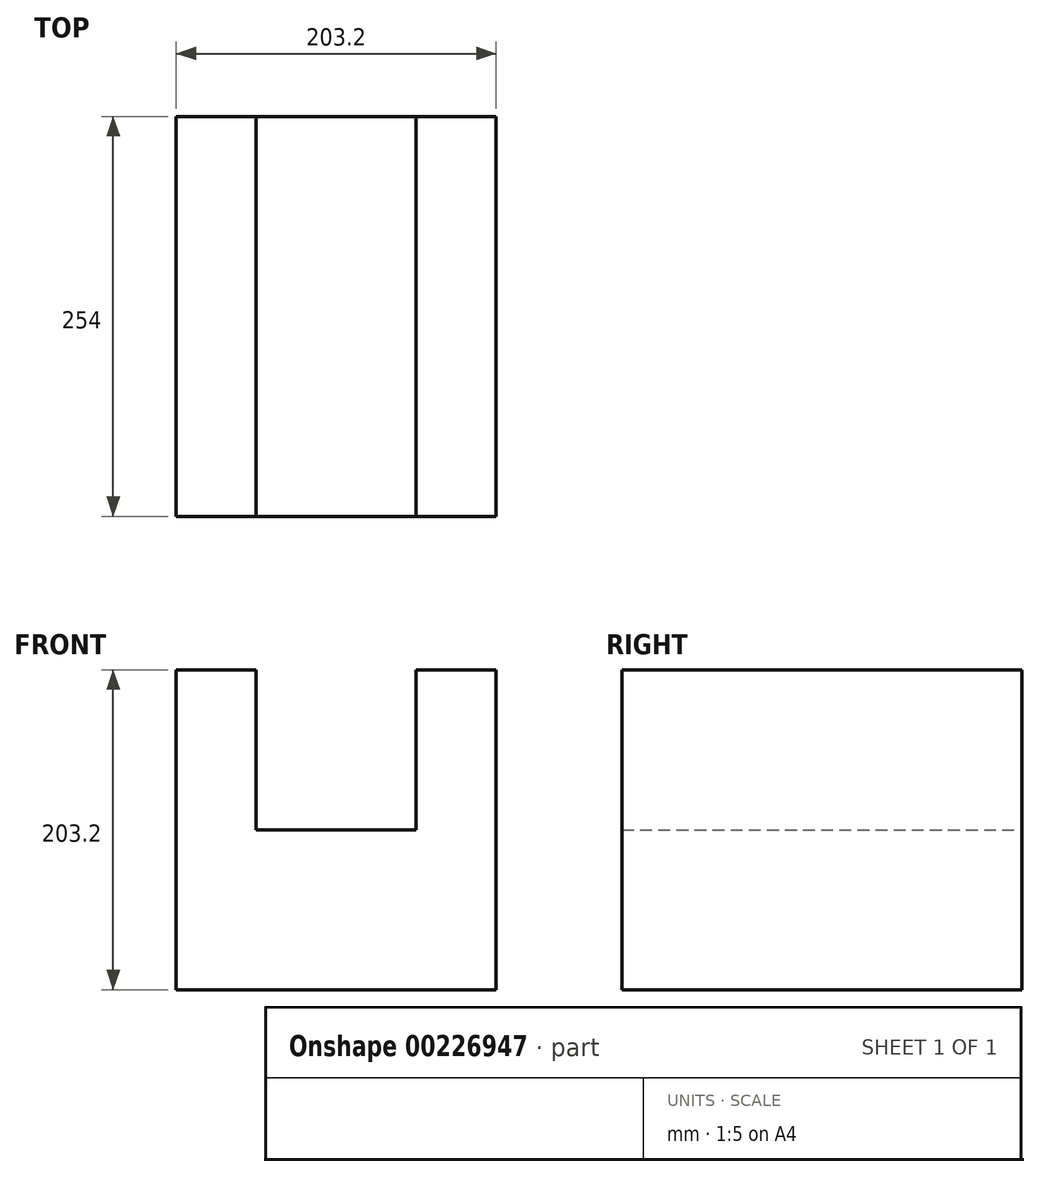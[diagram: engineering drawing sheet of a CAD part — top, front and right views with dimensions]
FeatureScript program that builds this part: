
annotation { "Feature Type Name" : "Feature", "Feature Type Description" : "" }
export const myFeature = defineFeature(function(context is Context, id is Id, definition is map)
    precondition{}
    {
        {
            var Q0;
            Q0=qCreatedBy(makeId("Front.planeOp"),FACE);
            var sketch = newSketch(context, id + "F0", { "sketchPlane" : qUnion([Q0])});
            skLineSegment(sketch, "E0", {"start": v(106.3, 82.24) * mm, "end": v(106.3, -120.96) * mm});
            skLineSegment(sketch, "E1", {"start": v(106.3, 82.24) * mm, "end": v(55.5, 82.24) * mm});
            skLineSegment(sketch, "E2", {"start": v(-96.9, 82.24) * mm, "end": v(-96.9, -120.96) * mm});
            skLineSegment(sketch, "E3", {"start": v(-96.9, -120.96) * mm, "end": v(106.3, -120.96) * mm});
            skLineSegment(sketch, "E4", {"start": v(-46.1, 82.24) * mm, "end": v(-46.1, -19.36) * mm});
            skLineSegment(sketch, "E5", {"start": v(55.5, 82.24) * mm, "end": v(55.5, -19.36) * mm});
            skLineSegment(sketch, "E6", {"start": v(-46.1, -19.36) * mm, "end": v(55.5, -19.36) * mm});
            skLineSegment(sketch, "E7.trimOffspring", {"start": v(-46.1, 82.24) * mm, "end": v(-96.9, 82.24) * mm});
            skSolve(sketch);
        }
        {
            var Q0;
            Q0=makeQuery(id+"F0.imprint","IMPRINT",FACE,{"disambiguationData":[TD([[makeQuery(id+"F0.imprint","IMPRINT",EDGE,{"derivedFrom":sQuery(id+"F0.wireOp",EDGE,"E0")}),-1.0]])]});
            extrude(context, id + "F1", {"entities" : qUnion([Q0]), "depth" : 254 * mm});
        }
    });
